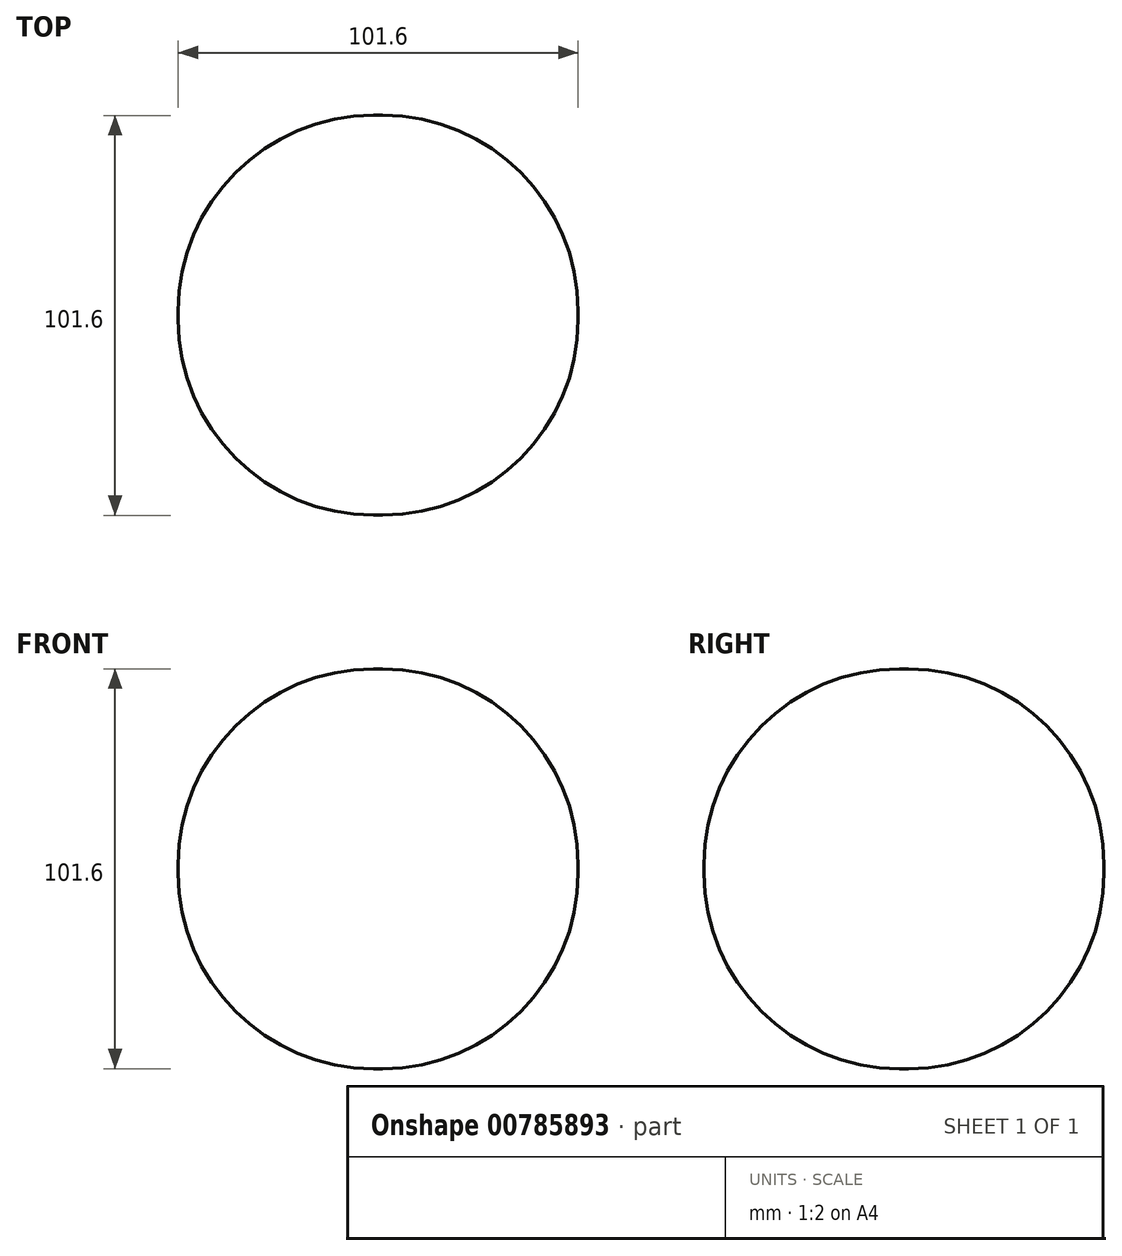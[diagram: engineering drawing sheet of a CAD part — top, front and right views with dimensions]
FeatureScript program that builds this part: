
annotation { "Feature Type Name" : "Feature", "Feature Type Description" : "" }
export const myFeature = defineFeature(function(context is Context, id is Id, definition is map)
    precondition{}
    {
        {
            var Q0;
            Q0=qCreatedBy(makeId("Right.planeOp"),FACE);
            var sketch = newSketch(context, id + "F0", { "sketchPlane" : qUnion([Q0])});
            skLineSegment(sketch, "E0.bottom", {"start": v(-35.17, 47.76) * mm, "end": v(66.43, 47.76) * mm});
            skLineSegment(sketch, "E0.top", {"start": v(-35.17, -53.84) * mm, "end": v(66.43, -53.84) * mm});
            skLineSegment(sketch, "E0.left", {"start": v(-35.17, 47.76) * mm, "end": v(-35.17, -53.84) * mm});
            skLineSegment(sketch, "E0.right", {"start": v(66.43, 47.76) * mm, "end": v(66.43, -53.84) * mm});
            skSolve(sketch);
        }
        {
            var Q0;
            Q0=makeQuery(id+"F0.imprint","IMPRINT",FACE,{"disambiguationData":[TD([[makeQuery(id+"F0.imprint","IMPRINT",EDGE,{"derivedFrom":sQuery(id+"F0.wireOp",EDGE,"E0.bottom")}),-1.0]])]});
            extrude(context, id + "F1", {"entities" : qUnion([Q0]), "depth" : 101.6 * mm, "offsetDistance" : 25.4 * mm});
        }
        {
            var Q0;
            Q0=makeQuery(id+"F1.opExtrude","SWEPT_FACE",FACE,{"disambiguationData":[OSD([sQuery(id+"F0.wireOp",EDGE,"E0.bottom")])]});
            var Q1;
            Q1=makeQuery(id+"F1.opExtrude","CAP_FACE",FACE,{"disambiguationData":[OSD([sQuery(id+"F0.wireOp",EDGE,"E0.bottom"),sQuery(id+"F0.wireOp",EDGE,"E0.top"),sQuery(id+"F0.wireOp",EDGE,"E0.left"),sQuery(id+"F0.wireOp",EDGE,"E0.right")])],"isStart":false});
            var Q2;
            Q2=makeQuery(id+"F1.opExtrude","SWEPT_FACE",FACE,{"disambiguationData":[OSD([sQuery(id+"F0.wireOp",EDGE,"E0.left")])]});
            var Q3;
            Q3=makeQuery(id+"F1.opExtrude","CAP_FACE",FACE,{"disambiguationData":[OSD([sQuery(id+"F0.wireOp",EDGE,"E0.bottom"),sQuery(id+"F0.wireOp",EDGE,"E0.top"),sQuery(id+"F0.wireOp",EDGE,"E0.left"),sQuery(id+"F0.wireOp",EDGE,"E0.right")])],"isStart":true});
            var Q4;
            Q4=makeQuery(id+"F1.opExtrude","SWEPT_FACE",FACE,{"disambiguationData":[OSD([sQuery(id+"F0.wireOp",EDGE,"E0.top")])]});
            fillet(context, id + "F2", {"entities" : qUnion([Q0, Q1, Q2, Q3, Q4]), "radius" : 49.67 * mm, "tangentPropagation" : true, "allowEdgeOverflow" : false});
        }
    });
